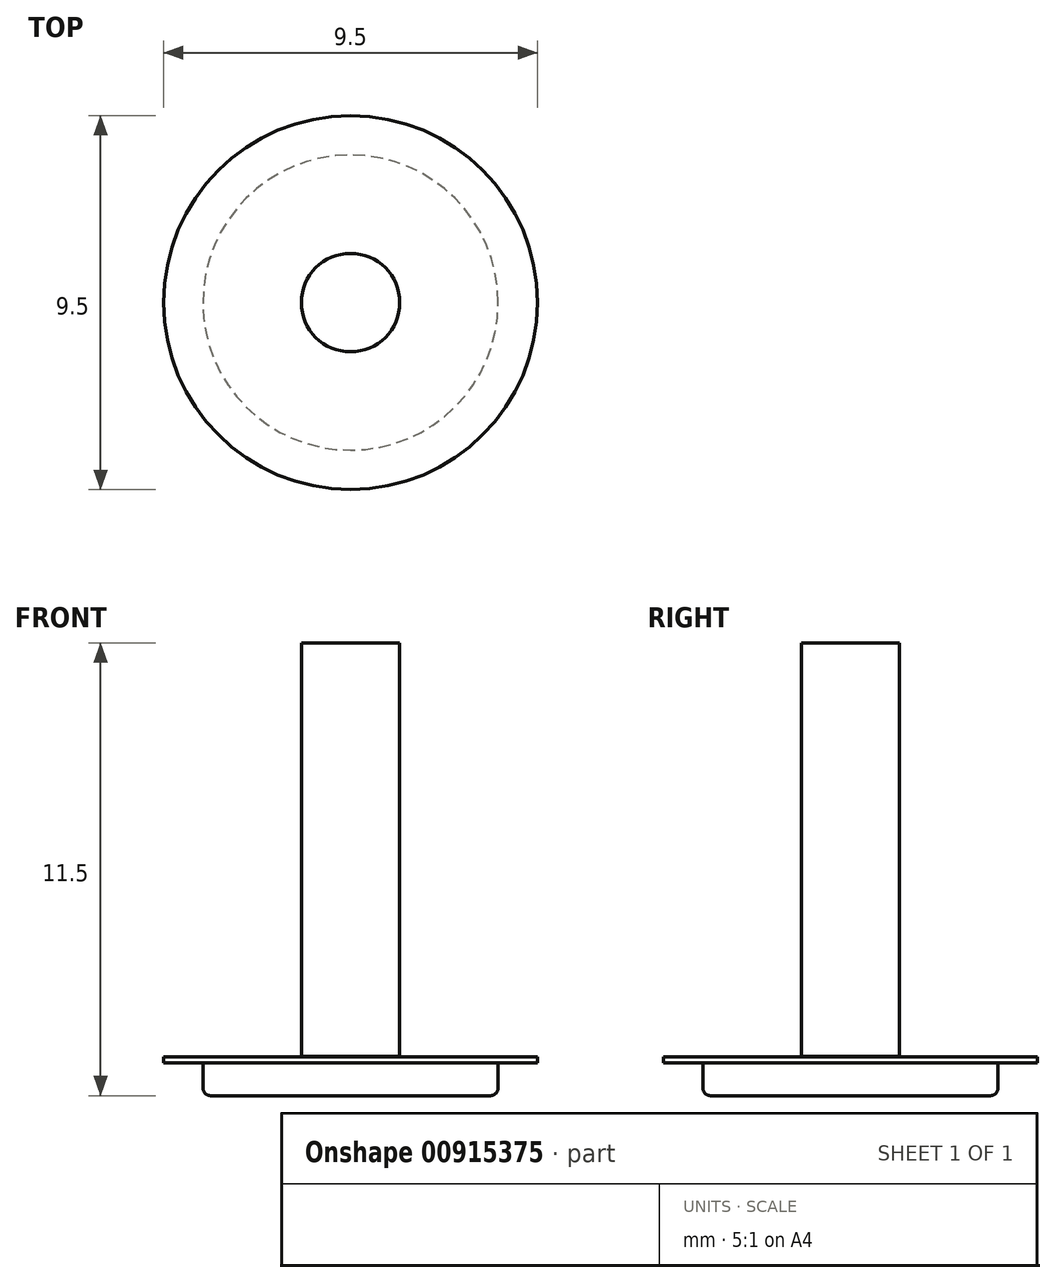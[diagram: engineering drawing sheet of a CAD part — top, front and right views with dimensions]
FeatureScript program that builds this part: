
annotation { "Feature Type Name" : "Feature", "Feature Type Description" : "" }
export const myFeature = defineFeature(function(context is Context, id is Id, definition is map)
    precondition{}
    {
        {
            var Q0;
            Q0=qCreatedBy(makeId("Top.planeOp"),FACE);
            var sketch = newSketch(context, id + "F0", { "sketchPlane" : qUnion([Q0])});
            skCircle(sketch, "E0", {"center": v(0, 0) * mm, "radius": 3.75 * mm});
            skCircle(sketch, "E1", {"center": v(0, 0) * mm, "radius": 4.75 * mm});
            skCircle(sketch, "E2", {"center": v(0, 0) * mm, "radius": 1.25 * mm});
            skSolve(sketch);
        }
        {
            var Q0;
            Q0=makeQuery(id+"F0.imprint","IMPRINT",FACE,{"disambiguationData":[TD([[makeQuery(id+"F0.imprint","IMPRINT",EDGE,{"derivedFrom":sQuery(id+"F0.wireOp",EDGE,"E0")}),1.0]])]});
            extrude(context, id + "F1", {"entities" : qUnion([Q0]), "depth" : 1 * mm, "offsetDistance" : 25.4 * mm});
        }
        {
            var Q0;
            Q0=makeQuery(id+"F0.imprint","IMPRINT",FACE,{"disambiguationData":[TD([[makeQuery(id+"F0.imprint","IMPRINT",EDGE,{"derivedFrom":sQuery(id+"F0.wireOp",EDGE,"E0")}),-1.0]])]});
            extrude(context, id + "F2", {"entities" : qUnion([Q0]), "operationType" : NewBodyOperationType.ADD, "depth" : 1 * mm, "offsetDistance" : 25.4 * mm, "hasSecondDirection" : true, "secondDirectionOppositeDirection" : false, "secondDirectionDepth" : 0.84 * mm});
        }
        {
            var Q0;
            Q0=makeQuery(id+"F0.imprint","IMPRINT",FACE,{"disambiguationData":[TD([[makeQuery(id+"F0.imprint","IMPRINT",EDGE,{"derivedFrom":sQuery(id+"F0.wireOp",EDGE,"E2")}),1.0]])]});
            extrude(context, id + "F3", {"entities" : qUnion([Q0]), "operationType" : NewBodyOperationType.ADD, "depth" : 11.5 * mm, "offsetDistance" : 25.4 * mm});
        }
        {
            var Q0;
            Q0=makeQuery(id+"F1.opExtrude","CAP_EDGE",EDGE,{"disambiguationData":[OSD([sQuery(id+"F0.wireOp",EDGE,"E0")])],"isStart":true});
            fillet(context, id + "F4", {"entities" : qUnion([Q0]), "radius" : .2 * mm, "tangentPropagation" : true, "allowEdgeOverflow" : false});
        }
    });
